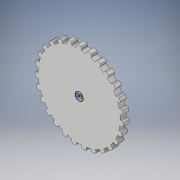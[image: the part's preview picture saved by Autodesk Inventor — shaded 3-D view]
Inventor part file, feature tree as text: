
AUTODESK INVENTOR PART (.ipt)
format: ipt  version: 2017 (Build 210142000, 142)  size: 396,800 bytes
history: native  units: in
note: dims shown in document units (in); Inventor stores cm internally (conversion verified against a paired STEP export)
features: sketch x4, extrude x3, pattern_circular x1
ambient origin geometry x8: Origin, YZ Plane, XZ Plane, XY Plane, X Axis, Y Axis, Z Axis, Center Point
bodies: Solid1 (feature_tree)
feature tree (8):
  extrude  "Extrusion1"  Depth=0.075in
  pattern_circular  "Circular Pattern1"  Count=108 Angle=360.0deg
  extrude  "Extrusion2"  Depth=0.062in
  sketch  "Sketch3"  dims[d6=0.04in d7=42.5197in d9=360.0deg]
  extrude  "Extrusion3"  Depth=0.15in TaperAngle=0.0deg
  sketch  "Sketch1"  dims[d0=2.025in d4=0.075in]
  sketch  "Sketch2"  dims[d5=0.04in]
  sketch  "Sketch4"  dims[d11=0.062in d12=0.062in d13=0.15in d14=0.0in d15=10.6299in d16=360.0deg d18=0.0591in d19=0.15in d20=0.0in d21=0.3862in d22=0.0in]
